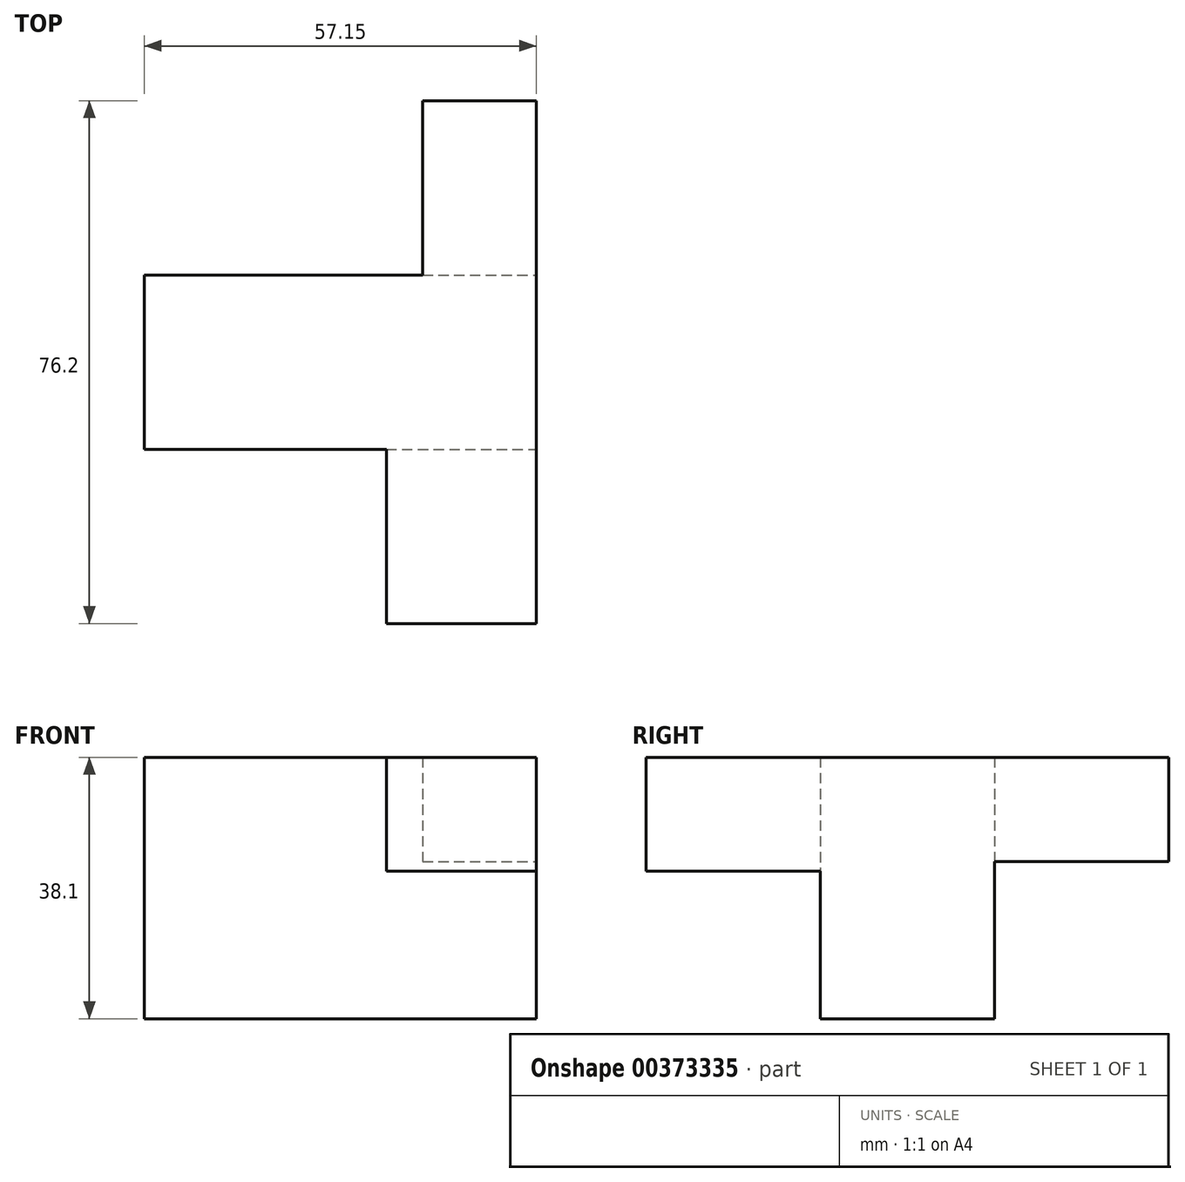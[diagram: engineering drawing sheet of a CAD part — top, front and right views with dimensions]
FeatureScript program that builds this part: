
annotation { "Feature Type Name" : "Feature", "Feature Type Description" : "" }
export const myFeature = defineFeature(function(context is Context, id is Id, definition is map)
    precondition{}
    {
        {
            var Q0;
            Q0=qCreatedBy(makeId("Front.planeOp"),FACE);
            var sketch = newSketch(context, id + "F0", { "sketchPlane" : qUnion([Q0])});
            skLineSegment(sketch, "E0", {"start": v(0, 38.1) * mm, "end": v(0, 0) * mm});
            skLineSegment(sketch, "E1", {"start": v(0, 0) * mm, "end": v(57.15, 0) * mm});
            skLineSegment(sketch, "E2", {"start": v(57.15, 0) * mm, "end": v(57.15, 38.1) * mm});
            skLineSegment(sketch, "E3", {"start": v(57.15, 38.1) * mm, "end": v(0, 38.1) * mm});
            skSolve(sketch);
        }
        {
            var Q0;
            Q0=makeQuery(id+"F0.imprint","IMPRINT",FACE,{"disambiguationData":[TD([[makeQuery(id+"F0.imprint","IMPRINT",EDGE,{"derivedFrom":sQuery(id+"F0.wireOp",EDGE,"E0")}),1.0]])]});
            extrude(context, id + "F1", {"entities" : qUnion([Q0]), "depth" : 25.4 * mm});
        }
        {
            var Q0;
            Q0=makeQuery(id+"F1.opExtrude","CAP_FACE",FACE,{"disambiguationData":[OSD([sQuery(id+"F0.wireOp",EDGE,"E0"),sQuery(id+"F0.wireOp",EDGE,"E1"),sQuery(id+"F0.wireOp",EDGE,"E2"),sQuery(id+"F0.wireOp",EDGE,"E3")])],"isStart":false});
            var sketch = newSketch(context, id + "F2", { "sketchPlane" : qUnion([Q0])});
            skLineSegment(sketch, "E4", {"start": v(35.28, 38.1) * mm, "end": v(35.28, 21.51) * mm});
            skLineSegment(sketch, "E5", {"start": v(35.28, 21.51) * mm, "end": v(57.15, 21.51) * mm});
            skSolve(sketch);
        }
        {
            var Q0;
            {var subQ0=sQuery(id+"F2.wireOp",EDGE,"E4");Q0=makeQuery(id+"F2.imprint","IMPRINT",FACE,{"disambiguationData":[TD([[makeQuery(id+"F2.imprint","IMPRINT",EDGE,{"derivedFrom":subQ0}),1.0]])]});}
            extrude(context, id + "F3", {"entities" : qUnion([Q0]), "operationType" : NewBodyOperationType.ADD, "depth" : 25.4 * mm});
        }
        {
            var Q0;
            Q0=makeQuery(id+"F1.opExtrude","CAP_FACE",FACE,{"disambiguationData":[OSD([sQuery(id+"F0.wireOp",EDGE,"E0"),sQuery(id+"F0.wireOp",EDGE,"E1"),sQuery(id+"F0.wireOp",EDGE,"E2"),sQuery(id+"F0.wireOp",EDGE,"E3")])],"isStart":true});
            var sketch = newSketch(context, id + "F4", { "sketchPlane" : qUnion([Q0])});
            skLineSegment(sketch, "E6", {"start": v(-40.57, 38.1) * mm, "end": v(-40.57, 22.87) * mm});
            skLineSegment(sketch, "E7", {"start": v(-40.57, 22.87) * mm, "end": v(-57.15, 22.87) * mm});
            skSolve(sketch);
        }
        {
            var Q0;
            {var subQ0=sQuery(id+"F4.wireOp",EDGE,"E6");Q0=makeQuery(id+"F4.imprint","IMPRINT",FACE,{"disambiguationData":[TD([[makeQuery(id+"F4.imprint","IMPRINT",EDGE,{"derivedFrom":subQ0}),-1.0]])]});}
            extrude(context, id + "F5", {"entities" : qUnion([Q0]), "operationType" : NewBodyOperationType.ADD, "depth" : 25.4 * mm});
        }
    });
